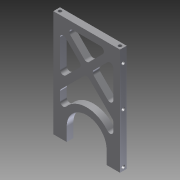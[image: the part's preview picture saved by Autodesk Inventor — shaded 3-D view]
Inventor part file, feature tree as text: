
AUTODESK INVENTOR PART (.ipt)
format: ipt  version: 2012 (Build 160160000, 160)  size: 199,168 bytes
history: native  units: in
note: dims shown in document units (in); Inventor stores cm internally (conversion verified against a paired STEP export)
features: sketch x5, hole x3, extrude x2, plane x1, fillet x1
ambient origin geometry x8: Origin, YZ Plane, XZ Plane, XY Plane, X Axis, Y Axis, Z Axis, Center Point
bodies: Solid1 (feature_tree)
feature tree (12):
  sketch  "Sketch1"  dims[d0=2.5in d1=1.25in]
  extrude  "Extrusion1"  Depth=1.25in
  hole  "Hole2"  [1 undecoded]
  hole  "Hole3"  [1 undecoded]
  hole  "Hole4"  [1 undecoded]
  plane  "Work Plane2"
  extrude  "Extrusion5"  Depth=0.125in
  fillet  "Fillet3"  Radius=0.125in
  sketch  "Sketch2"  dims[d2=4.0in d3=4.3435in]
  sketch  "Sketch3"  dims[d4=0.5in d5=0.5in]
  sketch  "Sketch5"  dims[d13=0.25in d14=0.0in d22=0.5in]
  sketch  "Sketch6"  dims[d23=0.125in d24=0.125in d25=0.125in d26=0.125in d27=0.75in d28=0.25in d29=0.25in d30=0.5635in d31=0.375in d32=0.8108in d33=0.125in d34=0.5in d35=0.125in d36=0.125in d37=0.125in d38=0.75in d39=0.25in d40=0.25in d41=0.5635in d42=0.375in d43=0.8108in d46=4.0in d52=0.5in d53=0.5in d54=2.0in d55=0.125in d56=2.0in d57=0.125in d78=0.125in d79=0.125in d80=0.125in d81=0.125in d82=0.75in d83=0.375in d84=0.25in d85=0.5635in d86=0.375in d87=0.8108in d98=-0.125in d99=1.0in d100=0.25in d101=0.25in d102=0.25in d103=45.0deg d104=0.25in d105=0.125in d106=0.125in d108=0.25in d109=0.125in d110=0.25in d111=0.125in d112=0.25in d113=0.125in d114=0.125in d115=0.125in d116=0.125in d117=1.0in d118=0.0in d119=0.125in]
note: 3 required parameter values undecoded (feature->parameter linkage not recoverable at this tier; creation-order binding heuristic only, values carry confidence <= 0.55)
